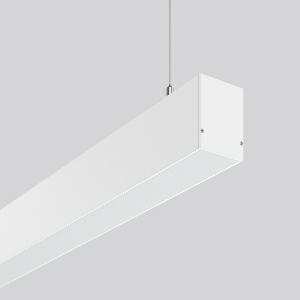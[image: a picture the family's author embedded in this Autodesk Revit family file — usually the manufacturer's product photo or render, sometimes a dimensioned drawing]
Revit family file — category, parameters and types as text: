
# Revit family: less_is_more_50_312321_002_76_785f
name_source: partatom
category: Lighting Fixtures
units: mm (PartAtom-declared; Revit-internal decimal feet)

## family parameters
Cut with Voids When Loaded = No
Host = Face
Light Source = No
Part Type = Normal
Room Calculation Point = No
Round Connector Dimension = Use Diameter
Shared = No

## types (1)
- LESS IS MORE 50 (1 x LED Modul 830, 8450 lm, 3000)
    Apparent Load = 74 VA
    CIE Flux Codes = 49 80 96 63 100
    Color Rendering = 80
    Color Temperature = 3000
    Default Elevation = 1800 mm
    Description = Series: LESS IS MORE 50
Linear pendant luminaire for aesthetically sophisticated lighting. Housing: extruded aluminium profile, powder-coated. End cap aluminium powder-coated. Canopy made of aluminium, powder-coated. Diffuser made of non-yellowing plastic (PMMA), opal. Direct 65%, indirect 35% light emission. Controlled separately. Suitable for pendant. 2-point steel cable suspension freely positionable and infinitely height-adjustable. Special lengths available on request. LED unit with integrated converter interchangeable and removable. Suitable for through-wiring. With sensors or as a safety luminaire on request. 
Colour: traffic white, matt (RAL 9016)
Length: 1967 mm
Width: 57 mm
Height: 75 mm
Suspension length: 2000 mm
Lamp: LED
Socket: without socket
Colour temperature: 3000K
Colour rendering index (CRI): 80
Light source: LED
Socket lamp2: Without base
Colour temperature: 3000K
System power: 74 W
Rated luminous flux: 8450 lm
Luminous efficiency: 114 lm/W
Control gear: Converter, dimmable, DALI
Control gear: Converter, dimmable, DALI
Protection class: I
Type of protection: IP 20
    Height = 75 mm
    Lamp = 1 x LED Modul 830
    Lamp Light Flux = 8450 lm
    Lamp count = 1
    Length = 1967 mm
    Lifetime = 50000 h
    Luminous efficacy = 114 lm/W
    Manufacturer = RZB
    ModVariant = No
    Model = 312321.002.76
    Mounting Place = Ceiling
    Mounting Type = Pendant
    Number of Poles = 1
    OnlyDefault = Yes
    Power Factor = 1
    Product Name = LESS IS MORE 50
    Product group = Pendant LED linear luminaires
    ProductGroupID = 907
    Protection Class = Protection class I
    Protection Degree = IP 20
    RLX_Detail_Level = 1
    RLX_Emergency_Light_Flux = 0 lm
    RLX_Emergency_Type = 0
    RLX_Emergency_Type_DB = No
    RlxData = <blob elided: 31685 chars, md5=d8212611>
    Socket = socket
    Standby Power = 0 W
    System Light Flux = 8450 lm
    System Power = 74 W
    Type Comments = Product without accessories
    Type Image = 312318.002.jpg
    URL = http://relux.com
    VarID = ---
    Voltage = 230 V
    Voltage Range = 220-240 V
    Weight = 0.00 kg
    Width = 57 mm

## geometry (parser evidence)
native form markers: Blend x4, Sweep x13
no freeform markers — native parametric forms only
